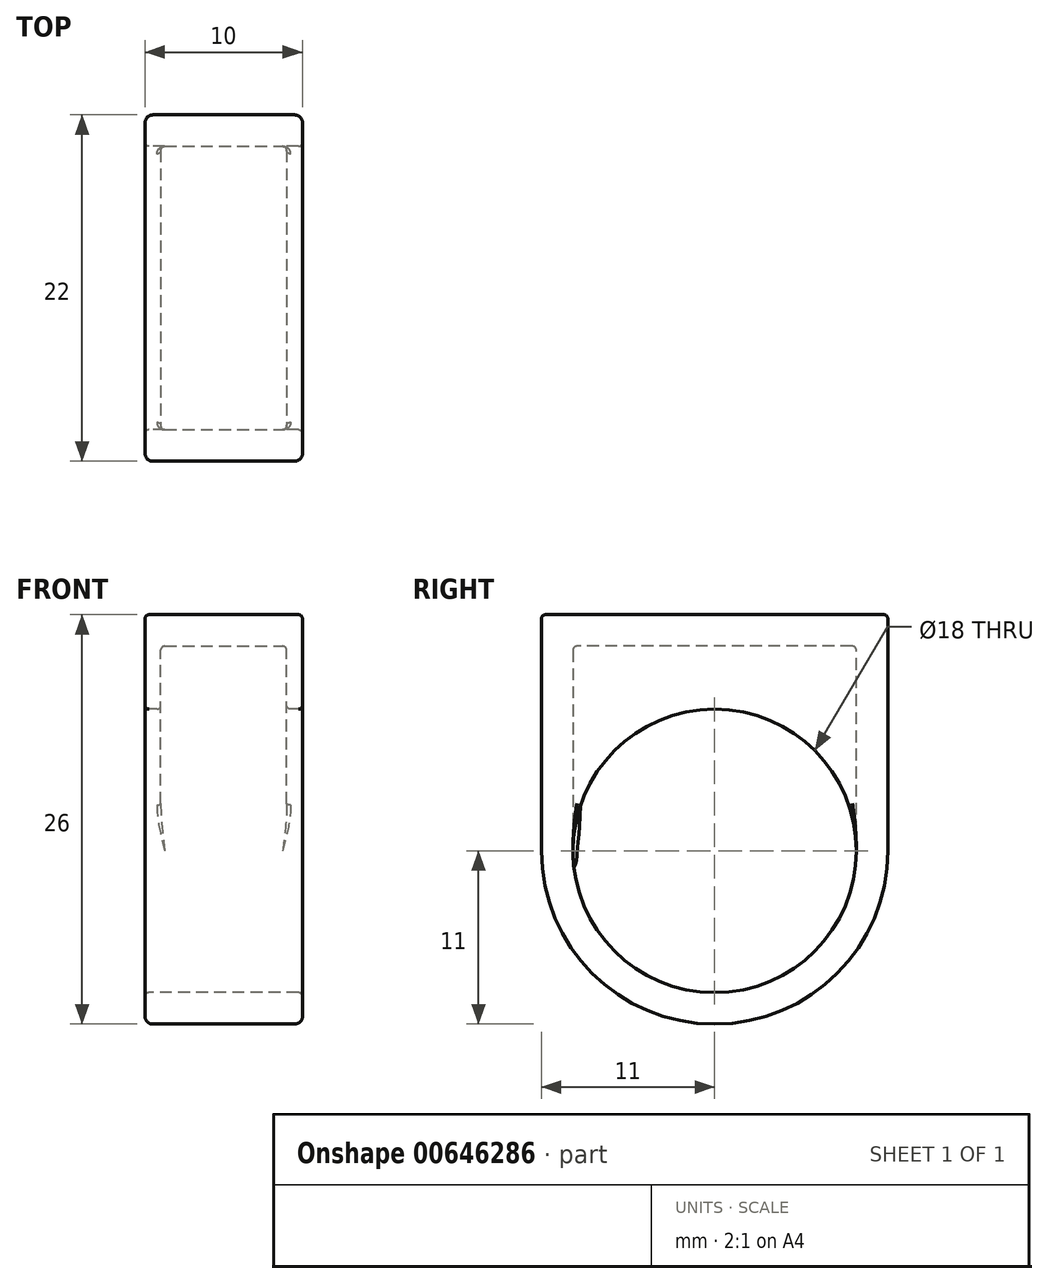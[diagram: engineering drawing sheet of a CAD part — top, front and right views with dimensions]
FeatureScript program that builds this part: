
annotation { "Feature Type Name" : "Feature", "Feature Type Description" : "" }
export const myFeature = defineFeature(function(context is Context, id is Id, definition is map)
    precondition{}
    {
        {
            var Q0;
            Q0=qCreatedBy(makeId("Right.planeOp"),FACE);
            var sketch = newSketch(context, id + "F0", { "sketchPlane" : qUnion([Q0])});
            skCircle(sketch, "E0", {"center": v(0, 0) * mm, "radius": 9 * mm});
            skCircle(sketch, "E1", {"center": v(0, 0) * mm, "radius": 11 * mm});
            skLineSegment(sketch, "E2", {"start": v(-11, 0) * mm, "end": v(-11, 15) * mm});
            skLineSegment(sketch, "E3", {"start": v(11, 0) * mm, "end": v(11, 15) * mm});
            skLineSegment(sketch, "E4", {"start": v(-11, 15) * mm, "end": v(11, 15) * mm});
            skSolve(sketch);
        }
        {
            var Q0;
            Q0 = qSketchRegion(id + "F0", true);
            extrude(context, id + "F1", {"entities" : qUnion([Q0]), "endBound" : BoundingType.SYMMETRIC, "depth" : 10 * mm, "offsetDistance" : 25 * mm});
        }
        {
            var Q0;
            Q0=qCreatedBy(makeId("Right.planeOp"),FACE);
            var sketch = newSketch(context, id + "F2", { "sketchPlane" : qUnion([Q0])});
            skLineSegment(sketch, "E5.0", {"start": v(-9, 13) * mm, "end": v(-9, 0) * mm});
            skLineSegment(sketch, "E5.1", {"start": v(9, 13) * mm, "end": v(-9, 13) * mm});
            skLineSegment(sketch, "E5.2", {"start": v(9, 0) * mm, "end": v(9, 13) * mm});
            skArc(sketch, "E5.3", {"start": v(-9, 0) * mm, "mid": v(0, -9) * mm, "end": v(9, 0) * mm});
            skSolve(sketch);
        }
        {
            var Q0;
            Q0 = qSketchRegion(id + "F2", true);
            extrude(context, id + "F3", {"entities" : qUnion([Q0]), "operationType" : NewBodyOperationType.REMOVE, "endBound" : BoundingType.SYMMETRIC, "oppositeDirection" : true, "depth" : 8 * mm, "offsetDistance" : 25 * mm});
        }
        {
            var Q0;
            Q0=makeQuery(id+"F1.opExtrude","CAP_EDGE",EDGE,{"disambiguationData":[OSD([sQuery(id+"F0.wireOp",EDGE,"E2")])],"isStart":false});
            var Q1;
            Q1=makeQuery(id+"F1.opExtrude","CAP_EDGE",EDGE,{"disambiguationData":[OSD([sQuery(id+"F0.wireOp",EDGE,"E2")])],"isStart":true});
            fillet(context, id + "F4", {"entities" : qUnion([Q0, Q1]), "radius" : 0.5 * mm, "tangentPropagation" : true, "allowEdgeOverflow" : false});
        }
        {
            var Q0;
            {var subQ0=sQuery(id+"F0.wireOp",EDGE,"E2");Q0=makeQuery(id+"F4.opFillet","BLEND_FACE",FACE,{"disambiguationData":[OSD([subQ0]),TDD([makeQuery(id+"F1.opExtrude","CAP_EDGE",EDGE,{"disambiguationData":[OSD([subQ0])],"isStart":false})])]});}
            var Q1;
            Q1=makeQuery(id+"F1.opExtrude","CAP_EDGE",EDGE,{"disambiguationData":[OSD([sQuery(id+"F0.wireOp",EDGE,"E0")])],"isStart":true});
            var Q2;
            Q2=makeQuery(id+"F1.opExtrude","SWEPT_EDGE",EDGE,{"disambiguationData":[OSD([sQuery(id+"F0.wireOp",EDGE,"E3"),sQuery(id+"F0.wireOp",EDGE,"E4")])]});
            var Q3;
            {var subQ0=sQuery(id+"F0.wireOp",EDGE,"E2");Q3=makeQuery(id+"F4.opFillet","BLEND_FACE",FACE,{"disambiguationData":[OSD([subQ0]),TDD([makeQuery(id+"F1.opExtrude","CAP_EDGE",EDGE,{"disambiguationData":[OSD([subQ0])],"isStart":true})])]});}
            var Q4;
            {var subQ0=sQuery(id+"F0.wireOp",EDGE,"E3");Q4=makeQuery(id+"F4.opFillet","BLEND_FACE",FACE,{"disambiguationData":[OSD([subQ0]),TDD([makeQuery(id+"F1.opExtrude","CAP_EDGE",EDGE,{"disambiguationData":[OSD([subQ0])],"isStart":false})])]});}
            var Q5;
            {var subQ0=sQuery(id+"F0.wireOp",EDGE,"E1");Q5=makeQuery(id+"F4.opFillet","BLEND_FACE",FACE,{"disambiguationData":[OSD([subQ0]),TDD([makeQuery(id+"F1.opExtrude","CAP_EDGE",EDGE,{"disambiguationData":[OSD([subQ0])],"isStart":false})])]});}
            var Q6;
            Q6=makeQuery(id+"F1.opExtrude","CAP_EDGE",EDGE,{"disambiguationData":[OSD([sQuery(id+"F0.wireOp",EDGE,"E0")])],"isStart":false});
            var Q7;
            Q7=makeQuery(id+"F1.opExtrude","SWEPT_EDGE",EDGE,{"disambiguationData":[OSD([sQuery(id+"F0.wireOp",EDGE,"E2"),sQuery(id+"F0.wireOp",EDGE,"E4")])]});
            var Q8;
            {var subQ0=sQuery(id+"F0.wireOp",EDGE,"E1");Q8=makeQuery(id+"F4.opFillet","BLEND_FACE",FACE,{"disambiguationData":[OSD([subQ0]),TDD([makeQuery(id+"F1.opExtrude","CAP_EDGE",EDGE,{"disambiguationData":[OSD([subQ0])],"isStart":true})])]});}
            var Q9;
            Q9=makeQuery(id+"F1.opExtrude","SWEPT_EDGE",EDGE,{"disambiguationData":[OSD([sQuery(id+"F0.wireOp",EDGE,"E1"),sQuery(id+"F0.wireOp",EDGE,"E2")])]});
            var Q10;
            Q10=makeQuery(id+"F3.boolean.opBoolean","COPY",FACE,{"derivedFrom":makeQuery(id+"F3.opExtrude","CAP_FACE",FACE,{"disambiguationData":[OSD([sQuery(id+"F2.wireOp",EDGE,"E5.0"),sQuery(id+"F2.wireOp",EDGE,"E5.1"),sQuery(id+"F2.wireOp",EDGE,"E5.2"),sQuery(id+"F2.wireOp",EDGE,"E5.3")])],"isStart":true})});
            var Q11;
            Q11=makeQuery(id+"F3.boolean.opBoolean","COPY",EDGE,{"derivedFrom":makeQuery(id+"F3.opExtrude","SWEPT_EDGE",EDGE,{"disambiguationData":[OSD([sQuery(id+"F2.wireOp",EDGE,"E5.2"),sQuery(id+"F2.wireOp",EDGE,"E5.3")])]})});
            var Q12;
            Q12=makeQuery(id+"F3.boolean.opBoolean","COPY",FACE,{"derivedFrom":makeQuery(id+"F3.opExtrude","SWEPT_FACE",FACE,{"disambiguationData":[OSD([sQuery(id+"F2.wireOp",EDGE,"E5.2")])]})});
            var Q13;
            Q13=makeQuery(id+"F1.opExtrude","SWEPT_FACE",FACE,{"disambiguationData":[OSD([sQuery(id+"F0.wireOp",EDGE,"E0")])]});
            var Q14;
            Q14=makeQuery(id+"F3.boolean.opBoolean","INTERSECT",EDGE,{"derivedFrom":[makeQuery(id+"F1.opExtrude","SWEPT_FACE",FACE,{"disambiguationData":[OSD([sQuery(id+"F0.wireOp",EDGE,"E0")])]}),makeQuery(id+"F3.opExtrude","CAP_FACE",FACE,{"disambiguationData":[OSD([sQuery(id+"F2.wireOp",EDGE,"E5.0"),sQuery(id+"F2.wireOp",EDGE,"E5.1"),sQuery(id+"F2.wireOp",EDGE,"E5.2"),sQuery(id+"F2.wireOp",EDGE,"E5.3")])],"isStart":true})]});
            var Q15;
            Q15=makeQuery(id+"F1.opExtrude","CAP_FACE",FACE,{"disambiguationData":[OSD([sQuery(id+"F0.wireOp",EDGE,"E0"),sQuery(id+"F0.wireOp",EDGE,"E1"),sQuery(id+"F0.wireOp",EDGE,"E2"),sQuery(id+"F0.wireOp",EDGE,"E3"),sQuery(id+"F0.wireOp",EDGE,"E4")])],"isStart":true});
            var Q16;
            {var subQ0=sQuery(id+"F0.wireOp",EDGE,"E1");Q16=makeQuery(id+"F4.opFillet","BLEND_EDGE",EDGE,{"blendedFrom":[makeQuery(id+"F1.opExtrude","CAP_EDGE",EDGE,{"disambiguationData":[OSD([subQ0])],"isStart":true}),makeQuery(id+"F1.opExtrude","SWEPT_FACE",FACE,{"disambiguationData":[OSD([subQ0])]})],"blendedInto":[makeQuery(id+"F1.opExtrude","SWEPT_FACE",FACE,{"disambiguationData":[OSD([subQ0])]})]});}
            var Q17;
            Q17=makeQuery(id+"F1.opExtrude","CAP_FACE",FACE,{"disambiguationData":[OSD([sQuery(id+"F0.wireOp",EDGE,"E0"),sQuery(id+"F0.wireOp",EDGE,"E1"),sQuery(id+"F0.wireOp",EDGE,"E2"),sQuery(id+"F0.wireOp",EDGE,"E3"),sQuery(id+"F0.wireOp",EDGE,"E4")])],"isStart":false});
            var Q18;
            Q18=makeQuery(id+"F4.opFillet","BLEND_EDGE",EDGE,{"blendedFrom":[makeQuery(id+"F1.opExtrude","CAP_EDGE",EDGE,{"disambiguationData":[OSD([sQuery(id+"F0.wireOp",EDGE,"E1")])],"isStart":false}),makeQuery(id+"F1.opExtrude","CAP_EDGE",EDGE,{"disambiguationData":[OSD([sQuery(id+"F0.wireOp",EDGE,"E2")])],"isStart":false})],"blendedInto":[]});
            var Q19;
            Q19=makeQuery(id+"F1.opExtrude","SWEPT_FACE",FACE,{"disambiguationData":[OSD([sQuery(id+"F0.wireOp",EDGE,"E1")])]});
            var Q20;
            Q20=makeQuery(id+"F1.opExtrude","SWEPT_FACE",FACE,{"disambiguationData":[OSD([sQuery(id+"F0.wireOp",EDGE,"E2")])]});
            var Q21;
            {var subQ0=sQuery(id+"F0.wireOp",EDGE,"E1");Q21=makeQuery(id+"F4.opFillet","BLEND_EDGE",EDGE,{"blendedFrom":[makeQuery(id+"F1.opExtrude","CAP_EDGE",EDGE,{"disambiguationData":[OSD([subQ0])],"isStart":false}),makeQuery(id+"F1.opExtrude","CAP_FACE",FACE,{"disambiguationData":[OSD([sQuery(id+"F0.wireOp",EDGE,"E0"),subQ0,sQuery(id+"F0.wireOp",EDGE,"E2"),sQuery(id+"F0.wireOp",EDGE,"E3"),sQuery(id+"F0.wireOp",EDGE,"E4")])],"isStart":false})],"blendedInto":[makeQuery(id+"F1.opExtrude","CAP_FACE",FACE,{"disambiguationData":[OSD([sQuery(id+"F0.wireOp",EDGE,"E0"),subQ0,sQuery(id+"F0.wireOp",EDGE,"E2"),sQuery(id+"F0.wireOp",EDGE,"E3"),sQuery(id+"F0.wireOp",EDGE,"E4")])],"isStart":false})]});}
            var Q22;
            Q22=makeQuery(id+"F1.opExtrude","SWEPT_FACE",FACE,{"disambiguationData":[OSD([sQuery(id+"F0.wireOp",EDGE,"E3")])]});
            var Q23;
            {var subQ0=sQuery(id+"F0.wireOp",EDGE,"E1");Q23=makeQuery(id+"F4.opFillet","BLEND_EDGE",EDGE,{"blendedFrom":[makeQuery(id+"F1.opExtrude","CAP_EDGE",EDGE,{"disambiguationData":[OSD([subQ0])],"isStart":false}),makeQuery(id+"F1.opExtrude","SWEPT_FACE",FACE,{"disambiguationData":[OSD([subQ0])]})],"blendedInto":[makeQuery(id+"F1.opExtrude","SWEPT_FACE",FACE,{"disambiguationData":[OSD([subQ0])]})]});}
            var Q24;
            Q24=makeQuery(id+"F1.opExtrude","SWEPT_FACE",FACE,{"disambiguationData":[OSD([sQuery(id+"F0.wireOp",EDGE,"E4")])]});
            var Q25;
            Q25=makeQuery(id+"F4.opFillet","BLEND_EDGE",EDGE,{"blendedFrom":[makeQuery(id+"F1.opExtrude","CAP_EDGE",EDGE,{"disambiguationData":[OSD([sQuery(id+"F0.wireOp",EDGE,"E2")])],"isStart":false}),makeQuery(id+"F1.opExtrude","SWEPT_FACE",FACE,{"disambiguationData":[OSD([sQuery(id+"F0.wireOp",EDGE,"E4")])]})],"blendedInto":[makeQuery(id+"F1.opExtrude","SWEPT_FACE",FACE,{"disambiguationData":[OSD([sQuery(id+"F0.wireOp",EDGE,"E4")])]})]});
            var Q26;
            Q26=makeQuery(id+"F1.opExtrude","CAP_EDGE",EDGE,{"disambiguationData":[OSD([sQuery(id+"F0.wireOp",EDGE,"E4")])],"isStart":true});
            var Q27;
            Q27=makeQuery(id+"F1.opExtrude","CAP_EDGE",EDGE,{"disambiguationData":[OSD([sQuery(id+"F0.wireOp",EDGE,"E4")])],"isStart":false});
            var Q28;
            {var subQ0=sQuery(id+"F0.wireOp",EDGE,"E3");Q28=makeQuery(id+"F4.opFillet","BLEND_FACE",FACE,{"disambiguationData":[OSD([subQ0]),TDD([makeQuery(id+"F1.opExtrude","CAP_EDGE",EDGE,{"disambiguationData":[OSD([subQ0])],"isStart":true})])]});}
            var Q29;
            Q29=makeQuery(id+"F1.opExtrude","SWEPT_EDGE",EDGE,{"disambiguationData":[OSD([sQuery(id+"F0.wireOp",EDGE,"E1"),sQuery(id+"F0.wireOp",EDGE,"E3")])]});
            var Q30;
            {var subQ0=sQuery(id+"F0.wireOp",EDGE,"E1");Q30=makeQuery(id+"F4.opFillet","BLEND_EDGE",EDGE,{"blendedFrom":[makeQuery(id+"F1.opExtrude","CAP_EDGE",EDGE,{"disambiguationData":[OSD([subQ0])],"isStart":true}),makeQuery(id+"F1.opExtrude","CAP_FACE",FACE,{"disambiguationData":[OSD([sQuery(id+"F0.wireOp",EDGE,"E0"),subQ0,sQuery(id+"F0.wireOp",EDGE,"E2"),sQuery(id+"F0.wireOp",EDGE,"E3"),sQuery(id+"F0.wireOp",EDGE,"E4")])],"isStart":true})],"blendedInto":[makeQuery(id+"F1.opExtrude","CAP_FACE",FACE,{"disambiguationData":[OSD([sQuery(id+"F0.wireOp",EDGE,"E0"),subQ0,sQuery(id+"F0.wireOp",EDGE,"E2"),sQuery(id+"F0.wireOp",EDGE,"E3"),sQuery(id+"F0.wireOp",EDGE,"E4")])],"isStart":true})]});}
            var Q31;
            {var subQ0=sQuery(id+"F0.wireOp",EDGE,"E2");Q31=makeQuery(id+"F4.opFillet","BLEND_EDGE",EDGE,{"blendedFrom":[makeQuery(id+"F1.opExtrude","CAP_EDGE",EDGE,{"disambiguationData":[OSD([subQ0])],"isStart":false}),makeQuery(id+"F1.opExtrude","CAP_FACE",FACE,{"disambiguationData":[OSD([sQuery(id+"F0.wireOp",EDGE,"E0"),sQuery(id+"F0.wireOp",EDGE,"E1"),subQ0,sQuery(id+"F0.wireOp",EDGE,"E3"),sQuery(id+"F0.wireOp",EDGE,"E4")])],"isStart":false})],"blendedInto":[makeQuery(id+"F1.opExtrude","CAP_FACE",FACE,{"disambiguationData":[OSD([sQuery(id+"F0.wireOp",EDGE,"E0"),sQuery(id+"F0.wireOp",EDGE,"E1"),subQ0,sQuery(id+"F0.wireOp",EDGE,"E3"),sQuery(id+"F0.wireOp",EDGE,"E4")])],"isStart":false})]});}
            var Q32;
            Q32=makeQuery(id+"F4.opFillet","BLEND_EDGE",EDGE,{"blendedFrom":[makeQuery(id+"F1.opExtrude","CAP_EDGE",EDGE,{"disambiguationData":[OSD([sQuery(id+"F0.wireOp",EDGE,"E2")])],"isStart":true}),makeQuery(id+"F1.opExtrude","SWEPT_FACE",FACE,{"disambiguationData":[OSD([sQuery(id+"F0.wireOp",EDGE,"E4")])]})],"blendedInto":[makeQuery(id+"F1.opExtrude","SWEPT_FACE",FACE,{"disambiguationData":[OSD([sQuery(id+"F0.wireOp",EDGE,"E4")])]})]});
            var Q33;
            {var subQ0=sQuery(id+"F0.wireOp",EDGE,"E2");Q33=makeQuery(id+"F4.opFillet","BLEND_EDGE",EDGE,{"blendedFrom":[makeQuery(id+"F1.opExtrude","CAP_EDGE",EDGE,{"disambiguationData":[OSD([subQ0])],"isStart":true}),makeQuery(id+"F1.opExtrude","SWEPT_FACE",FACE,{"disambiguationData":[OSD([subQ0])]})],"blendedInto":[makeQuery(id+"F1.opExtrude","SWEPT_FACE",FACE,{"disambiguationData":[OSD([subQ0])]})]});}
            var Q34;
            Q34=makeQuery(id+"F3.boolean.opBoolean","COPY",EDGE,{"derivedFrom":makeQuery(id+"F3.opExtrude","SWEPT_EDGE",EDGE,{"disambiguationData":[OSD([sQuery(id+"F2.wireOp",EDGE,"E5.0"),sQuery(id+"F2.wireOp",EDGE,"E5.1")])]})});
            var Q35;
            Q35=makeQuery(id+"F3.boolean.opBoolean","COPY",FACE,{"derivedFrom":makeQuery(id+"F3.opExtrude","SWEPT_FACE",FACE,{"disambiguationData":[OSD([sQuery(id+"F2.wireOp",EDGE,"E5.0")])]})});
            var Q36;
            Q36=makeQuery(id+"F3.boolean.opBoolean","COPY",EDGE,{"derivedFrom":makeQuery(id+"F3.opExtrude","SWEPT_EDGE",EDGE,{"disambiguationData":[OSD([sQuery(id+"F2.wireOp",EDGE,"E5.0"),sQuery(id+"F2.wireOp",EDGE,"E5.3")])]})});
            var Q37;
            Q37=makeQuery(id+"F3.boolean.opBoolean","COPY",EDGE,{"derivedFrom":makeQuery(id+"F3.opExtrude","SWEPT_EDGE",EDGE,{"disambiguationData":[OSD([sQuery(id+"F2.wireOp",EDGE,"E5.1"),sQuery(id+"F2.wireOp",EDGE,"E5.2")])]})});
            var Q38;
            Q38=makeQuery(id+"F3.boolean.opBoolean","COPY",FACE,{"derivedFrom":makeQuery(id+"F3.opExtrude","CAP_FACE",FACE,{"disambiguationData":[OSD([sQuery(id+"F2.wireOp",EDGE,"E5.0"),sQuery(id+"F2.wireOp",EDGE,"E5.1"),sQuery(id+"F2.wireOp",EDGE,"E5.2"),sQuery(id+"F2.wireOp",EDGE,"E5.3")])],"isStart":false})});
            var Q39;
            Q39=makeQuery(id+"F3.boolean.opBoolean","COPY",FACE,{"derivedFrom":makeQuery(id+"F3.opExtrude","SWEPT_FACE",FACE,{"disambiguationData":[OSD([sQuery(id+"F2.wireOp",EDGE,"E5.1")])]})});
            var Q40;
            Q40=makeQuery(id+"F3.boolean.opBoolean","COPY",EDGE,{"derivedFrom":makeQuery(id+"F3.opExtrude","CAP_EDGE",EDGE,{"disambiguationData":[OSD([sQuery(id+"F2.wireOp",EDGE,"E5.1")])],"isStart":true})});
            var Q41;
            Q41=makeQuery(id+"F3.boolean.opBoolean","COPY",EDGE,{"derivedFrom":makeQuery(id+"F3.opExtrude","CAP_EDGE",EDGE,{"disambiguationData":[OSD([sQuery(id+"F2.wireOp",EDGE,"E5.1")])],"isStart":false})});
            var Q42;
            Q42=makeQuery(id+"F3.boolean.opBoolean","COPY",EDGE,{"derivedFrom":makeQuery(id+"F3.opExtrude","CAP_EDGE",EDGE,{"disambiguationData":[OSD([sQuery(id+"F2.wireOp",EDGE,"E5.2")])],"isStart":true})});
            var Q43;
            Q43=makeQuery(id+"F3.boolean.opBoolean","COPY",EDGE,{"derivedFrom":makeQuery(id+"F3.opExtrude","CAP_EDGE",EDGE,{"disambiguationData":[OSD([sQuery(id+"F2.wireOp",EDGE,"E5.2")])],"isStart":false})});
            var Q44;
            Q44=makeQuery(id+"F3.boolean.opBoolean","INTERSECT",EDGE,{"derivedFrom":[makeQuery(id+"F1.opExtrude","SWEPT_FACE",FACE,{"disambiguationData":[OSD([sQuery(id+"F0.wireOp",EDGE,"E0")])]}),makeQuery(id+"F3.opExtrude","CAP_FACE",FACE,{"disambiguationData":[OSD([sQuery(id+"F2.wireOp",EDGE,"E5.0"),sQuery(id+"F2.wireOp",EDGE,"E5.1"),sQuery(id+"F2.wireOp",EDGE,"E5.2"),sQuery(id+"F2.wireOp",EDGE,"E5.3")])],"isStart":false})]});
            var Q45;
            Q45=makeQuery(id+"F4.opFillet","BLEND_EDGE",EDGE,{"blendedFrom":[makeQuery(id+"F1.opExtrude","CAP_EDGE",EDGE,{"disambiguationData":[OSD([sQuery(id+"F0.wireOp",EDGE,"E1")])],"isStart":false}),makeQuery(id+"F1.opExtrude","CAP_EDGE",EDGE,{"disambiguationData":[OSD([sQuery(id+"F0.wireOp",EDGE,"E3")])],"isStart":false})],"blendedInto":[]});
            var Q46;
            {var subQ0=sQuery(id+"F0.wireOp",EDGE,"E2");Q46=makeQuery(id+"F4.opFillet","BLEND_EDGE",EDGE,{"blendedFrom":[makeQuery(id+"F1.opExtrude","CAP_EDGE",EDGE,{"disambiguationData":[OSD([subQ0])],"isStart":false}),makeQuery(id+"F1.opExtrude","SWEPT_FACE",FACE,{"disambiguationData":[OSD([subQ0])]})],"blendedInto":[makeQuery(id+"F1.opExtrude","SWEPT_FACE",FACE,{"disambiguationData":[OSD([subQ0])]})]});}
            var Q47;
            {var subQ0=sQuery(id+"F0.wireOp",EDGE,"E3");Q47=makeQuery(id+"F4.opFillet","BLEND_EDGE",EDGE,{"blendedFrom":[makeQuery(id+"F1.opExtrude","CAP_EDGE",EDGE,{"disambiguationData":[OSD([subQ0])],"isStart":true}),makeQuery(id+"F1.opExtrude","CAP_FACE",FACE,{"disambiguationData":[OSD([sQuery(id+"F0.wireOp",EDGE,"E0"),sQuery(id+"F0.wireOp",EDGE,"E1"),sQuery(id+"F0.wireOp",EDGE,"E2"),subQ0,sQuery(id+"F0.wireOp",EDGE,"E4")])],"isStart":true})],"blendedInto":[makeQuery(id+"F1.opExtrude","CAP_FACE",FACE,{"disambiguationData":[OSD([sQuery(id+"F0.wireOp",EDGE,"E0"),sQuery(id+"F0.wireOp",EDGE,"E1"),sQuery(id+"F0.wireOp",EDGE,"E2"),subQ0,sQuery(id+"F0.wireOp",EDGE,"E4")])],"isStart":true})]});}
            var Q48;
            {var subQ0=sQuery(id+"F0.wireOp",EDGE,"E3");Q48=makeQuery(id+"F4.opFillet","BLEND_EDGE",EDGE,{"blendedFrom":[makeQuery(id+"F1.opExtrude","CAP_EDGE",EDGE,{"disambiguationData":[OSD([subQ0])],"isStart":true}),makeQuery(id+"F1.opExtrude","SWEPT_FACE",FACE,{"disambiguationData":[OSD([subQ0])]})],"blendedInto":[makeQuery(id+"F1.opExtrude","SWEPT_FACE",FACE,{"disambiguationData":[OSD([subQ0])]})]});}
            var Q49;
            Q49=makeQuery(id+"F4.opFillet","BLEND_EDGE",EDGE,{"blendedFrom":[makeQuery(id+"F1.opExtrude","CAP_EDGE",EDGE,{"disambiguationData":[OSD([sQuery(id+"F0.wireOp",EDGE,"E3")])],"isStart":true}),makeQuery(id+"F1.opExtrude","SWEPT_FACE",FACE,{"disambiguationData":[OSD([sQuery(id+"F0.wireOp",EDGE,"E4")])]})],"blendedInto":[makeQuery(id+"F1.opExtrude","SWEPT_FACE",FACE,{"disambiguationData":[OSD([sQuery(id+"F0.wireOp",EDGE,"E4")])]})]});
            var Q50;
            {var subQ0=sQuery(id+"F0.wireOp",EDGE,"E3");Q50=makeQuery(id+"F4.opFillet","BLEND_EDGE",EDGE,{"blendedFrom":[makeQuery(id+"F1.opExtrude","CAP_EDGE",EDGE,{"disambiguationData":[OSD([subQ0])],"isStart":false}),makeQuery(id+"F1.opExtrude","CAP_FACE",FACE,{"disambiguationData":[OSD([sQuery(id+"F0.wireOp",EDGE,"E0"),sQuery(id+"F0.wireOp",EDGE,"E1"),sQuery(id+"F0.wireOp",EDGE,"E2"),subQ0,sQuery(id+"F0.wireOp",EDGE,"E4")])],"isStart":false})],"blendedInto":[makeQuery(id+"F1.opExtrude","CAP_FACE",FACE,{"disambiguationData":[OSD([sQuery(id+"F0.wireOp",EDGE,"E0"),sQuery(id+"F0.wireOp",EDGE,"E1"),sQuery(id+"F0.wireOp",EDGE,"E2"),subQ0,sQuery(id+"F0.wireOp",EDGE,"E4")])],"isStart":false})]});}
            var Q51;
            Q51=makeQuery(id+"F4.opFillet","BLEND_EDGE",EDGE,{"blendedFrom":[makeQuery(id+"F1.opExtrude","CAP_EDGE",EDGE,{"disambiguationData":[OSD([sQuery(id+"F0.wireOp",EDGE,"E3")])],"isStart":false}),makeQuery(id+"F1.opExtrude","SWEPT_FACE",FACE,{"disambiguationData":[OSD([sQuery(id+"F0.wireOp",EDGE,"E4")])]})],"blendedInto":[makeQuery(id+"F1.opExtrude","SWEPT_FACE",FACE,{"disambiguationData":[OSD([sQuery(id+"F0.wireOp",EDGE,"E4")])]})]});
            var Q52;
            Q52=makeQuery(id+"F4.opFillet","BLEND_EDGE",EDGE,{"blendedFrom":[makeQuery(id+"F1.opExtrude","CAP_EDGE",EDGE,{"disambiguationData":[OSD([sQuery(id+"F0.wireOp",EDGE,"E1")])],"isStart":true}),makeQuery(id+"F1.opExtrude","CAP_EDGE",EDGE,{"disambiguationData":[OSD([sQuery(id+"F0.wireOp",EDGE,"E2")])],"isStart":true})],"blendedInto":[]});
            var Q53;
            Q53=makeQuery(id+"F4.opFillet","BLEND_EDGE",EDGE,{"blendedFrom":[makeQuery(id+"F1.opExtrude","CAP_EDGE",EDGE,{"disambiguationData":[OSD([sQuery(id+"F0.wireOp",EDGE,"E1")])],"isStart":true}),makeQuery(id+"F1.opExtrude","CAP_EDGE",EDGE,{"disambiguationData":[OSD([sQuery(id+"F0.wireOp",EDGE,"E3")])],"isStart":true})],"blendedInto":[]});
            var Q54;
            Q54=makeQuery(id+"F3.boolean.opBoolean","COPY",EDGE,{"derivedFrom":makeQuery(id+"F3.opExtrude","CAP_EDGE",EDGE,{"disambiguationData":[OSD([sQuery(id+"F2.wireOp",EDGE,"E5.0")])],"isStart":true})});
            var Q55;
            Q55=makeQuery(id+"F3.boolean.opBoolean","COPY",EDGE,{"derivedFrom":makeQuery(id+"F3.opExtrude","CAP_EDGE",EDGE,{"disambiguationData":[OSD([sQuery(id+"F2.wireOp",EDGE,"E5.0")])],"isStart":false})});
            var Q56;
            {var subQ0=sQuery(id+"F0.wireOp",EDGE,"E2");Q56=makeQuery(id+"F4.opFillet","BLEND_EDGE",EDGE,{"blendedFrom":[makeQuery(id+"F1.opExtrude","CAP_EDGE",EDGE,{"disambiguationData":[OSD([subQ0])],"isStart":true}),makeQuery(id+"F1.opExtrude","CAP_FACE",FACE,{"disambiguationData":[OSD([sQuery(id+"F0.wireOp",EDGE,"E0"),sQuery(id+"F0.wireOp",EDGE,"E1"),subQ0,sQuery(id+"F0.wireOp",EDGE,"E3"),sQuery(id+"F0.wireOp",EDGE,"E4")])],"isStart":true})],"blendedInto":[makeQuery(id+"F1.opExtrude","CAP_FACE",FACE,{"disambiguationData":[OSD([sQuery(id+"F0.wireOp",EDGE,"E0"),sQuery(id+"F0.wireOp",EDGE,"E1"),subQ0,sQuery(id+"F0.wireOp",EDGE,"E3"),sQuery(id+"F0.wireOp",EDGE,"E4")])],"isStart":true})]});}
            var Q57;
            {var subQ0=sQuery(id+"F0.wireOp",EDGE,"E3");Q57=makeQuery(id+"F4.opFillet","BLEND_EDGE",EDGE,{"blendedFrom":[makeQuery(id+"F1.opExtrude","CAP_EDGE",EDGE,{"disambiguationData":[OSD([subQ0])],"isStart":false}),makeQuery(id+"F1.opExtrude","SWEPT_FACE",FACE,{"disambiguationData":[OSD([subQ0])]})],"blendedInto":[makeQuery(id+"F1.opExtrude","SWEPT_FACE",FACE,{"disambiguationData":[OSD([subQ0])]})]});}
            fillet(context, id + "F5", {"entities" : qUnion([Q0, Q1, Q2, Q3, Q4, Q5, Q6, Q7, Q8, Q9, Q10, Q11, Q12, Q13, Q14, Q15, Q16, Q17, Q18, Q19, Q20, Q21, Q22, Q23, Q24, Q25, Q26, Q27, Q28, Q29, Q30, Q31, Q32, Q33, Q34, Q35, Q36, Q37, Q38, Q39, Q40, Q41, Q42, Q43, Q44, Q45, Q46, Q47, Q48, Q49, Q50, Q51, Q52, Q53, Q54, Q55, Q56, Q57]), "radius" : 0.25 * mm, "tangentPropagation" : true, "allowEdgeOverflow" : false});
        }
    });
